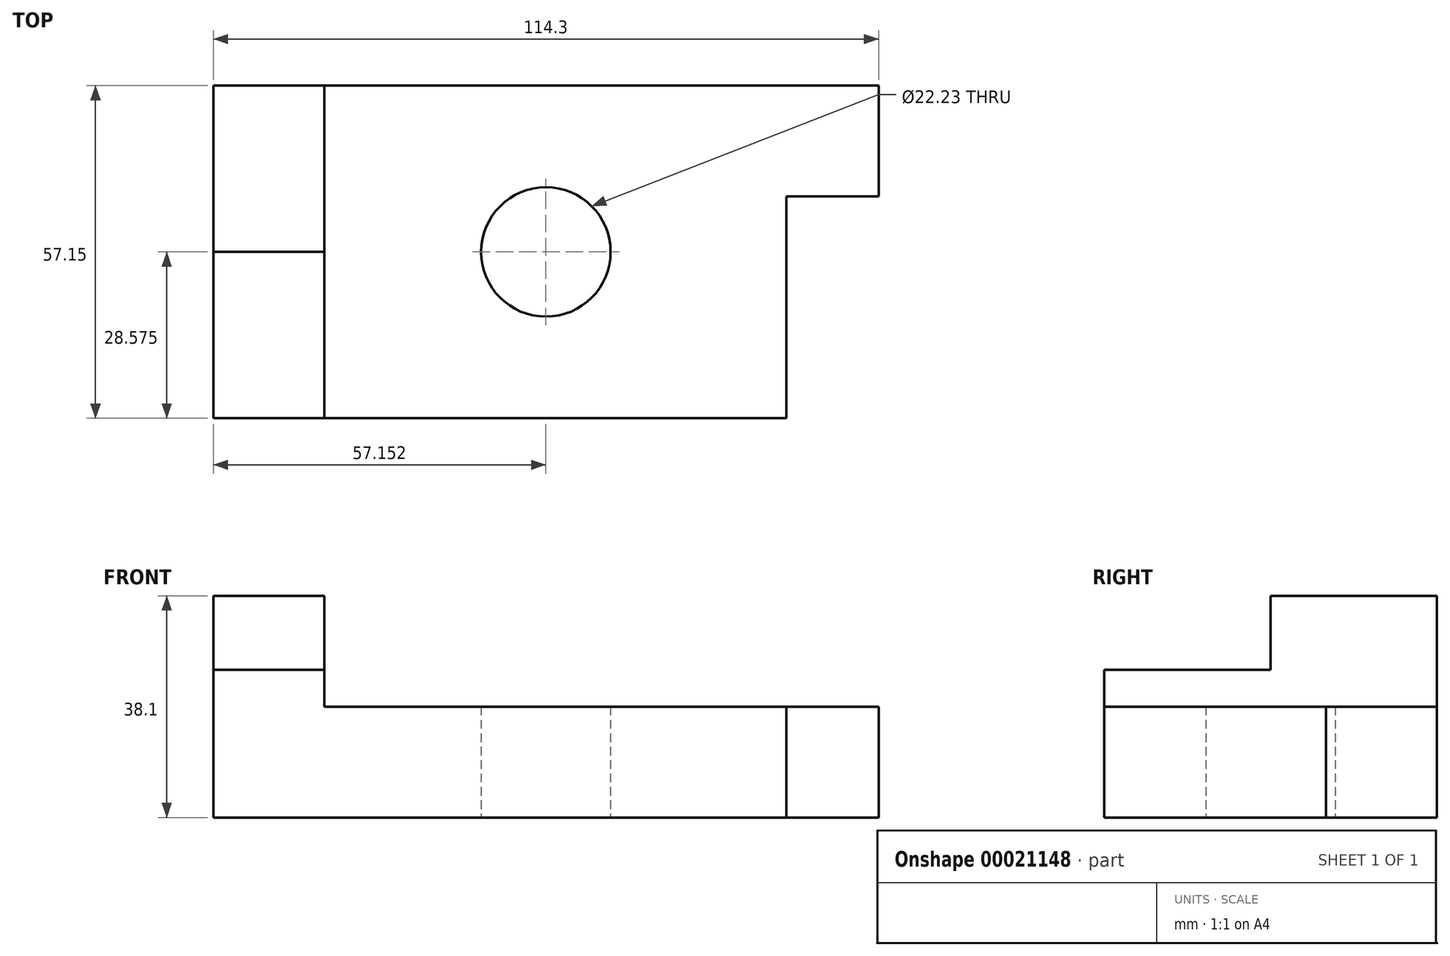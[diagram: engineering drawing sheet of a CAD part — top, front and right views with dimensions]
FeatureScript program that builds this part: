
annotation { "Feature Type Name" : "Feature", "Feature Type Description" : "" }
export const myFeature = defineFeature(function(context is Context, id is Id, definition is map)
    precondition{}
    {
        {
            var Q0;
            Q0=qCreatedBy(makeId("Top.planeOp"),FACE);
            var sketch = newSketch(context, id + "F0", { "sketchPlane" : qUnion([Q0])});
            skLineSegment(sketch, "E0.bottom", {"start": v(-66.39, -38.1) * mm, "end": v(32.04, -38.1) * mm});
            skLineSegment(sketch, "E0.top", {"start": v(-66.39, 19.05) * mm, "end": v(47.91, 19.05) * mm});
            skLineSegment(sketch, "E0.left", {"start": v(-66.39, -38.1) * mm, "end": v(-66.39, 19.05) * mm});
            skLineSegment(sketch, "E0.right", {"start": v(47.91, 0) * mm, "end": v(47.91, 19.05) * mm});
            skLineSegment(sketch, "E1.top", {"start": v(47.91, 0) * mm, "end": v(32.04, 0) * mm});
            skLineSegment(sketch, "E1.right", {"start": v(32.04, -38.1) * mm, "end": v(32.04, 0) * mm});
            skCircle(sketch, "E2", {"center": v(-9.24, -9.52) * mm, "radius": 11.11 * mm});
            skSolve(sketch);
        }
        {
            var Q0;
            Q0=makeQuery(id+"F0.imprint","IMPRINT",FACE,{"disambiguationData":[TD([[makeQuery(id+"F0.imprint","IMPRINT",EDGE,{"derivedFrom":sQuery(id+"F0.wireOp",EDGE,"E0.bottom")}),1.0]])]});
            extrude(context, id + "F1", {"entities" : qUnion([Q0]), "depth" : 19.05 * mm});
        }
        {
            var Q0;
            Q0=makeQuery(id+"F1.opExtrude","CAP_FACE",FACE,{"disambiguationData":[OSD([sQuery(id+"F0.wireOp",EDGE,"E0.bottom"),sQuery(id+"F0.wireOp",EDGE,"E0.top"),sQuery(id+"F0.wireOp",EDGE,"E0.left"),sQuery(id+"F0.wireOp",EDGE,"E0.right"),sQuery(id+"F0.wireOp",EDGE,"E1.top"),sQuery(id+"F0.wireOp",EDGE,"E1.right"),sQuery(id+"F0.wireOp",EDGE,"E2")])],"isStart":false});
            var sketch = newSketch(context, id + "F2", { "sketchPlane" : qUnion([Q0])});
            skLineSegment(sketch, "E3.left", {"start": v(-66.39, 19.05) * mm, "end": v(-66.39, -45.73) * mm});
            skLineSegment(sketch, "E4.bottom", {"start": v(-66.39, 19.05) * mm, "end": v(-47.34, 19.05) * mm});
            skLineSegment(sketch, "E4.top", {"start": v(-66.39, -9.53) * mm, "end": v(-47.34, -9.53) * mm});
            skLineSegment(sketch, "E4.left", {"start": v(-66.39, 19.05) * mm, "end": v(-66.39, -9.53) * mm});
            skLineSegment(sketch, "E4.right", {"start": v(-47.34, 19.05) * mm, "end": v(-47.34, -9.53) * mm});
            skSolve(sketch);
        }
        {
            var Q0;
            Q0=makeQuery(id+"F2.imprint","IMPRINT",FACE,{"disambiguationData":[TD([[makeQuery(id+"F2.imprint","IMPRINT",EDGE,{"derivedFrom":sQuery(id+"F2.wireOp",EDGE,"E4.bottom")}),-1.0]])]});
            extrude(context, id + "F3", {"entities" : qUnion([Q0]), "operationType" : NewBodyOperationType.ADD, "depth" : 19.05 * mm});
        }
        {
            var Q0;
            Q0=makeQuery(id+"F1.opExtrude","CAP_FACE",FACE,{"disambiguationData":[OSD([sQuery(id+"F0.wireOp",EDGE,"E0.bottom"),sQuery(id+"F0.wireOp",EDGE,"E0.top"),sQuery(id+"F0.wireOp",EDGE,"E0.left"),sQuery(id+"F0.wireOp",EDGE,"E0.right"),sQuery(id+"F0.wireOp",EDGE,"E1.top"),sQuery(id+"F0.wireOp",EDGE,"E1.right"),sQuery(id+"F0.wireOp",EDGE,"E2")])],"isStart":false});
            var sketch = newSketch(context, id + "F4", { "sketchPlane" : qUnion([Q0])});
            skLineSegment(sketch, "E5.bottom", {"start": v(-66.39, -38.1) * mm, "end": v(-47.34, -38.1) * mm});
            skLineSegment(sketch, "E5.top", {"start": v(-66.39, -9.53) * mm, "end": v(-47.34, -9.53) * mm});
            skLineSegment(sketch, "E5.left", {"start": v(-66.39, -38.1) * mm, "end": v(-66.39, -9.53) * mm});
            skLineSegment(sketch, "E5.right", {"start": v(-47.34, -38.1) * mm, "end": v(-47.34, -9.53) * mm});
            skSolve(sketch);
        }
        {
            var Q0;
            Q0=makeQuery(id+"F4.imprint","IMPRINT",FACE,{"disambiguationData":[TD([[makeQuery(id+"F4.imprint","IMPRINT",EDGE,{"derivedFrom":sQuery(id+"F4.wireOp",EDGE,"E5.bottom")}),1.0]])]});
            extrude(context, id + "F5", {"entities" : qUnion([Q0]), "operationType" : NewBodyOperationType.ADD, "depth" : 6.35 * mm});
        }
    });
